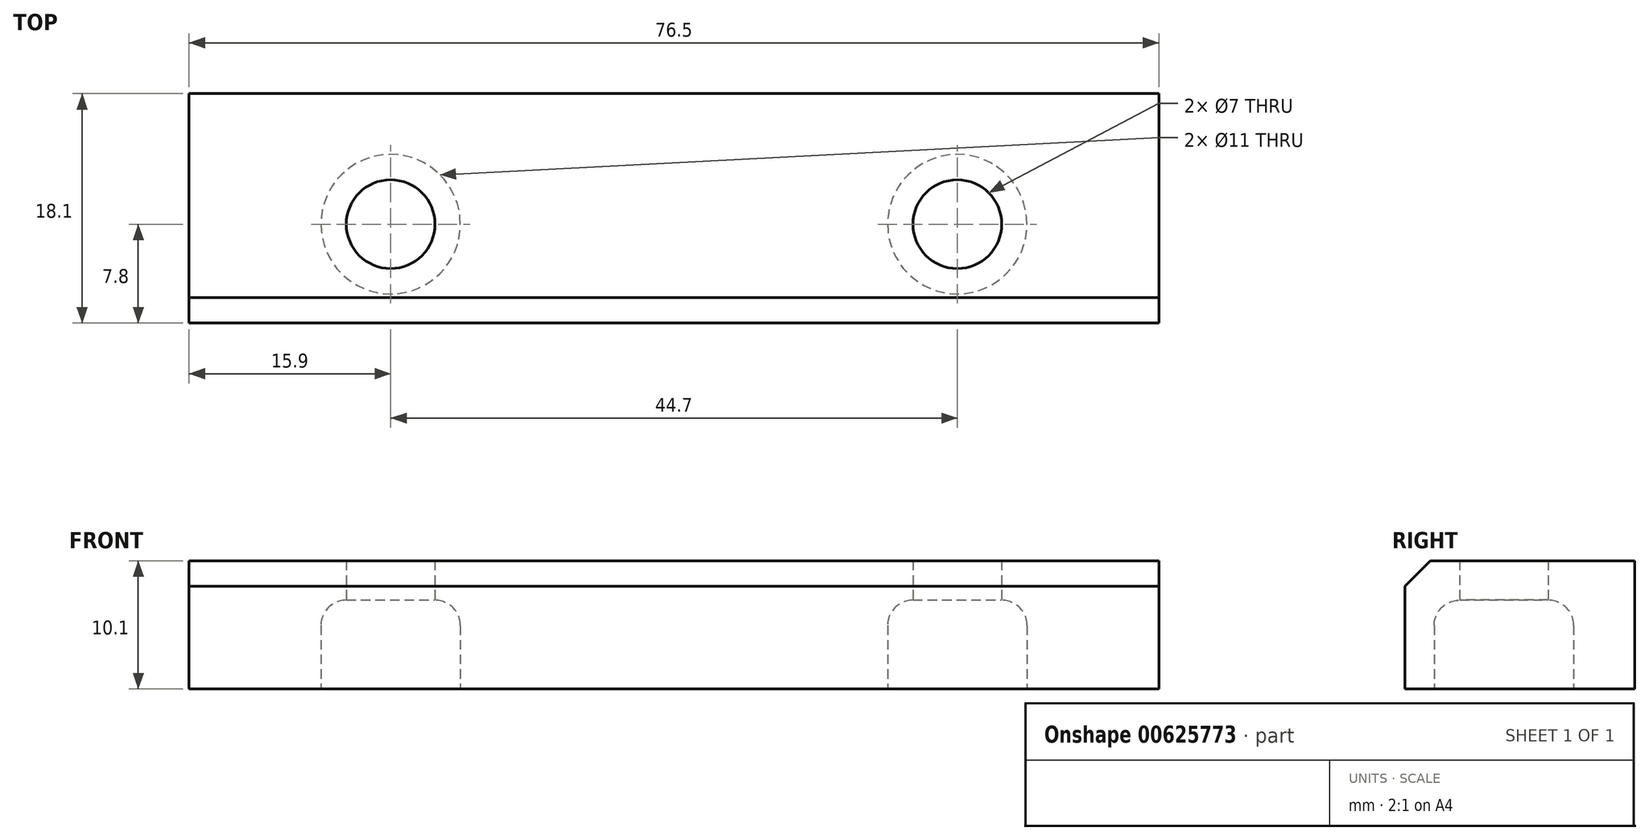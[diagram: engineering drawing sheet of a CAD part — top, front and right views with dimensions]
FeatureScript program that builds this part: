
annotation { "Feature Type Name" : "Feature", "Feature Type Description" : "" }
export const myFeature = defineFeature(function(context is Context, id is Id, definition is map)
    precondition{}
    {
        {
            var Q0;
            Q0=qCreatedBy(makeId("Top.planeOp"),FACE);
            var sketch = newSketch(context, id + "F0", { "sketchPlane" : qUnion([Q0])});
            skLineSegment(sketch, "E0.bottom", {"start": v(0, 0) * mm, "end": v(76.5, 0) * mm});
            skLineSegment(sketch, "E0.top", {"start": v(0, -18.1) * mm, "end": v(76.5, -18.1) * mm});
            skLineSegment(sketch, "E0.left", {"start": v(0, 0) * mm, "end": v(0, -18.1) * mm});
            skLineSegment(sketch, "E0.right", {"start": v(76.5, 0) * mm, "end": v(76.5, -18.1) * mm});
            skCircle(sketch, "E1", {"center": v(60.6, -10.3) * mm, "radius": 3.5 * mm});
            skPoint(sketch, "E2", {"position": v(38.25, 0) * mm});
            skLineSegment(sketch, "E3", {"start": v(38.25, 11.18) * mm, "end": v(38.25, -23.87) * mm, "construction": true});
            skPoint(sketch, "E3.endSnap0", {"position": v(38.25, -18.1) * mm});
            skCircle(sketch, "E4.MirrorC", {"center": v(15.9, -10.3) * mm, "radius": 3.5 * mm});
            skSolve(sketch);
        }
        {
            var Q0;
            Q0 = qSketchRegion(id + "F0", true);
            extrude(context, id + "F1", {"entities" : qUnion([Q0]), "depth" : 10.1 * mm, "offsetDistance" : 25 * mm});
        }
        {
            var Q0;
            Q0=makeQuery(id+"F1.opExtrude","CAP_FACE",FACE,{"disambiguationData":[OSD([sQuery(id+"F0.wireOp",EDGE,"E0.bottom"),sQuery(id+"F0.wireOp",EDGE,"E0.top"),sQuery(id+"F0.wireOp",EDGE,"E0.left"),sQuery(id+"F0.wireOp",EDGE,"E0.right"),sQuery(id+"F0.wireOp",EDGE,"Bk1rPu7d-v7hq-K7nN-9VoD-55qIeHuxggjs"),sQuery(id+"F0.wireOp",EDGE,"E1")])],"isStart":true});
            var sketch = newSketch(context, id + "F2", { "sketchPlane" : qUnion([Q0])});
            skCircle(sketch, "E5", {"center": v(60.6, 10.3) * mm, "radius": 5.5 * mm});
            skPoint(sketch, "E6", {"position": v(38.25, 0) * mm});
            skLineSegment(sketch, "E7", {"start": v(38.25, -11.37) * mm, "end": v(38.25, 23.12) * mm, "construction": true});
            skPoint(sketch, "E7.endSnap0", {"position": v(38.25, 18.1) * mm});
            skCircle(sketch, "E8.MirrorC", {"center": v(15.9, 10.3) * mm, "radius": 5.5 * mm});
            skSolve(sketch);
        }
        {
            var Q0;
            Q0 = qSketchRegion(id + "F2", true);
            extrude(context, id + "F3", {"entities" : qUnion([Q0]), "operationType" : NewBodyOperationType.REMOVE, "oppositeDirection" : true, "depth" : 7 * mm, "offsetDistance" : 25 * mm});
        }
        {
            var Q0;
            Q0=makeQuery(id+"F3.boolean.opBoolean","COPY",EDGE,{"derivedFrom":makeQuery(id+"F3.opExtrude","CAP_EDGE",EDGE,{"disambiguationData":[OSD([sQuery(id+"F2.wireOp",EDGE,"skoUkyCn-68iL-IKfC-M4jx-QS8Q8x68Kf3P")])],"isStart":false})});
            var Q1;
            Q1=makeQuery(id+"F3.boolean.opBoolean","COPY",EDGE,{"derivedFrom":makeQuery(id+"F3.opExtrude","CAP_EDGE",EDGE,{"disambiguationData":[OSD([sQuery(id+"F2.wireOp",EDGE,"E5")])],"isStart":false})});
            var Q2;
            Q2=makeQuery(id+"F3.boolean.opBoolean","COPY",EDGE,{"derivedFrom":makeQuery(id+"F3.opExtrude","CAP_EDGE",EDGE,{"disambiguationData":[OSD([sQuery(id+"F2.wireOp",EDGE,"E8.MirrorC")])],"isStart":false})});
            fillet(context, id + "F4", {"entities" : qUnion([Q0, Q1, Q2]), "radius" : 2 * mm, "tangentPropagation" : true, "allowEdgeOverflow" : false});
        }
        {
            var Q0;
            Q0=makeQuery(id+"F1.opExtrude","CAP_EDGE",EDGE,{"disambiguationData":[OSD([sQuery(id+"F0.wireOp",EDGE,"E0.top")])],"isStart":false});
            chamfer(context, id + "F5", {"entities" : qUnion([Q0]), "width" : 2 * mm, "tangentPropagation" : true});
        }
    });
